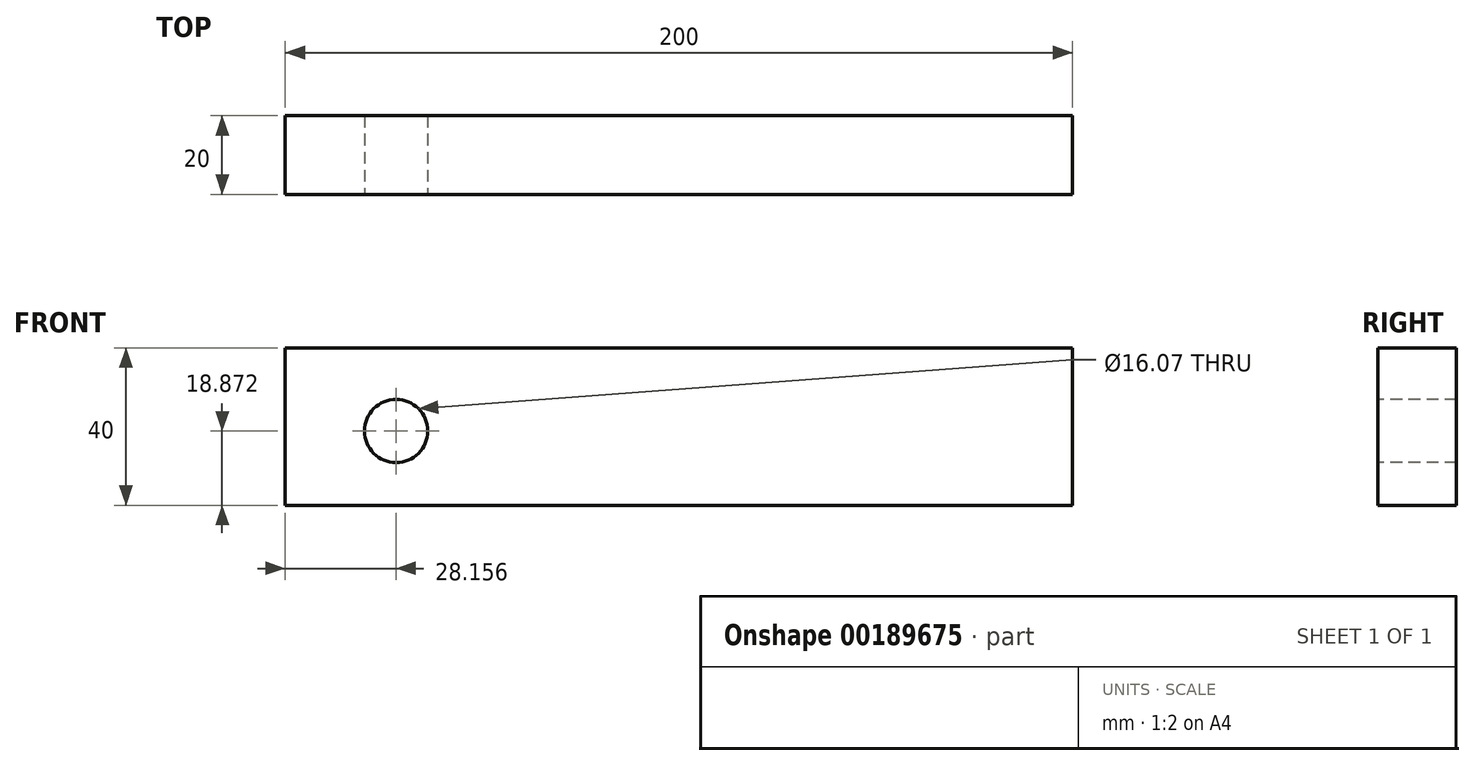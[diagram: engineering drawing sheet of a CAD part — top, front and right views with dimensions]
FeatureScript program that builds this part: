
annotation { "Feature Type Name" : "Feature", "Feature Type Description" : "" }
export const myFeature = defineFeature(function(context is Context, id is Id, definition is map)
    precondition{}
    {
        {
            var Q0;
            Q0=qCreatedBy(makeId("Front.planeOp"),FACE);
            var sketch = newSketch(context, id + "F0", { "sketchPlane" : qUnion([Q0])});
            skLineSegment(sketch, "E0.bottom", {"start": v(0, 40) * mm, "end": v(200, 40) * mm});
            skLineSegment(sketch, "E0.top", {"start": v(0, 0) * mm, "end": v(200, 0) * mm});
            skLineSegment(sketch, "E0.left", {"start": v(0, 40) * mm, "end": v(0, 0) * mm});
            skLineSegment(sketch, "E0.right", {"start": v(200, 40) * mm, "end": v(200, 0) * mm});
            skSolve(sketch);
        }
        {
            var Q0;
            Q0 = qSketchRegion(id + "F0", true);
            extrude(context, id + "F1", {"entities" : qUnion([Q0]), "depth" : 20 * mm});
        }
        {
            var Q0;
            Q0=makeQuery(id+"F1.opExtrude","CAP_FACE",FACE,{"disambiguationData":[OSD([sQuery(id+"F0.wireOp",EDGE,"E0.bottom"),sQuery(id+"F0.wireOp",EDGE,"E0.top"),sQuery(id+"F0.wireOp",EDGE,"E0.left"),sQuery(id+"F0.wireOp",EDGE,"E0.right")])],"isStart":false});
            var sketch = newSketch(context, id + "F2", { "sketchPlane" : qUnion([Q0])});
            skCircle(sketch, "E1", {"center": v(28.16, 18.87) * mm, "radius": 8.04 * mm});
            skSolve(sketch);
        }
        {
            var Q0;
            Q0=makeQuery(id+"F2.imprint","IMPRINT",FACE,{"disambiguationData":[TD([[makeQuery(id+"F2.imprint","IMPRINT",EDGE,{"derivedFrom":sQuery(id+"F2.wireOp",EDGE,"E1")}),1.0]])]});
            var Q1;
            Q1=sQuery(id+"F2.wireOp",EDGE,"E1");
            extrude(context, id + "F3", {"entities" : qUnion([Q0]), "operationType" : NewBodyOperationType.REMOVE, "surfaceEntities" : qUnion([Q1]), "oppositeDirection" : true, "depth" : 25 * mm});
        }
    });
